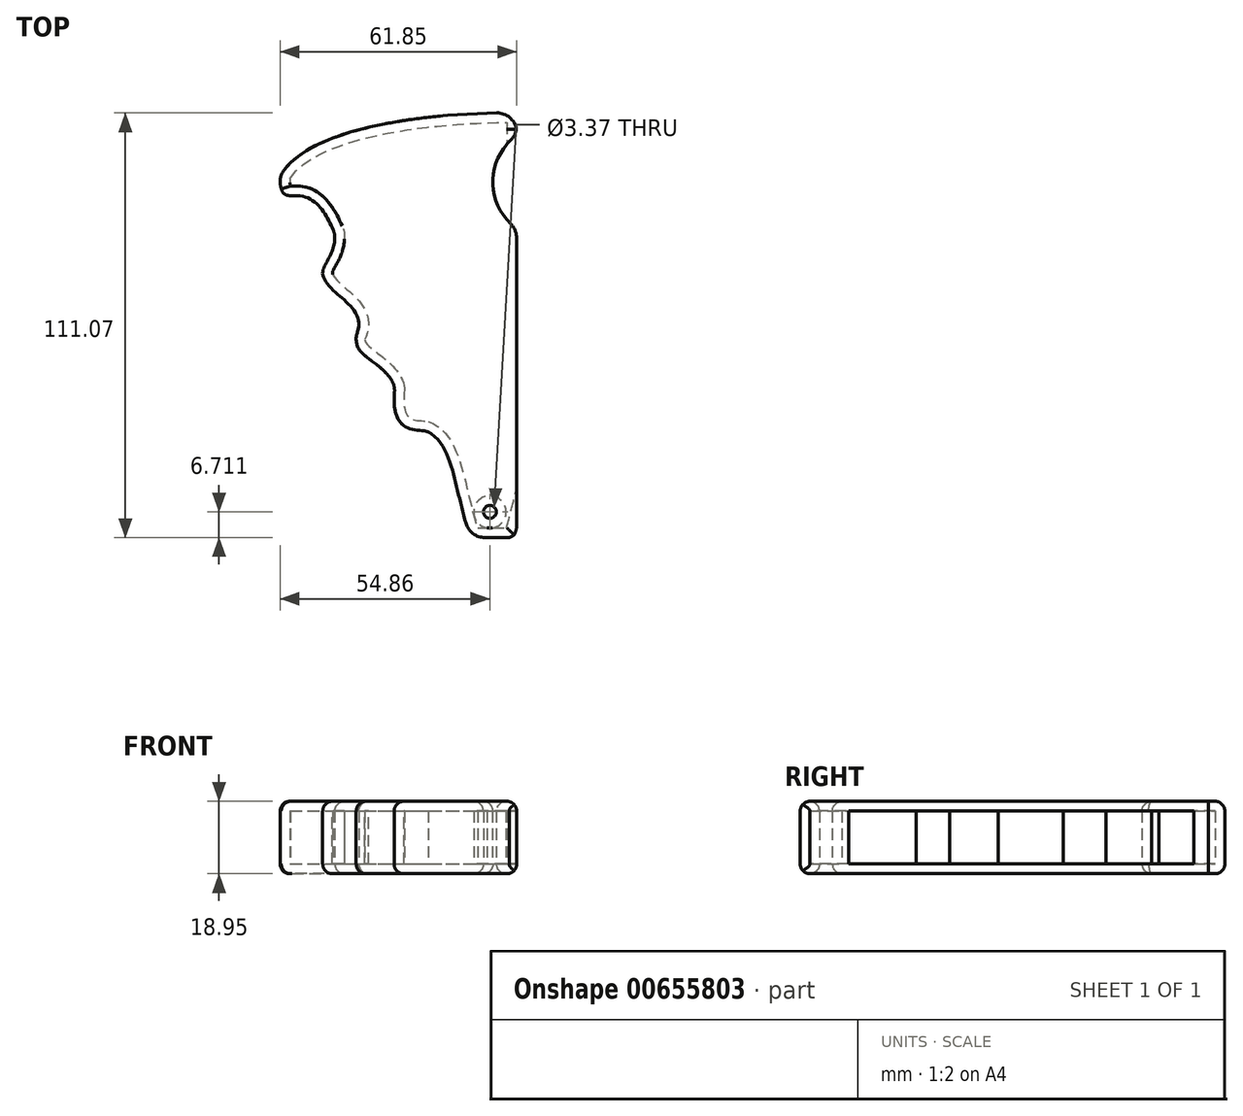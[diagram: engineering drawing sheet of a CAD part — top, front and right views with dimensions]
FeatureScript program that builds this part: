
annotation { "Feature Type Name" : "Feature", "Feature Type Description" : "" }
export const myFeature = defineFeature(function(context is Context, id is Id, definition is map)
    precondition{}
    {
        {
            var Q0;
            Q0=qCreatedBy(makeId("Top.planeOp"),FACE);
            var sketch = newSketch(context, id + "F0", { "sketchPlane" : qUnion([Q0])});
            skLineSegment(sketch, "E0.bottom", {"start": v(-30.91, 55.7) * mm, "end": v(31, 55.7) * mm});
            skLineSegment(sketch, "E0.top", {"start": v(-30.91, -55.42) * mm, "end": v(31, -55.42) * mm});
            skLineSegment(sketch, "E0.left", {"start": v(-30.91, 55.7) * mm, "end": v(-30.91, -55.42) * mm});
            skLineSegment(sketch, "E0.right", {"start": v(31, 55.7) * mm, "end": v(31, -55.42) * mm});
            skPoint(sketch, "E1", {"position": v(-30.91, 39.04) * mm});
            skPoint(sketch, "E2", {"position": v(31, 50.15) * mm});
            skPoint(sketch, "E3", {"position": v(31, 24.75) * mm});
            skCircle(sketch, "E4", {"center": v(40.03, 37.59) * mm, "radius": 15.24 * mm});
            skFitSpline(sketch, "E5", {"points": [v(-30.91, 39.04) * mm, v(31, 55.7) * mm], "startDerivative": vector(17.2, 32.72) * mm, "endDerivative": vector(93, 0) * mm});
            skFitSpline(sketch, "E6", {"points": [v(-30.91, 39.04) * mm, v(-16.57, 24.07) * mm], "startDerivative": vector(0, -34.25) * mm, "endDerivative": vector(21.47, -53.67) * mm});
            skFitSpline(sketch, "E7", {"points": [v(-16.57, 24.07) * mm, v(-19.33, 12.26) * mm], "startDerivative": vector(1.02, -19.93) * mm, "endDerivative": vector(5.41, -10.48) * mm});
            skFitSpline(sketch, "E8", {"points": [v(-19.33, 12.26) * mm, v(-11.02, -2.64) * mm], "startDerivative": vector(7.14, -14.54) * mm, "endDerivative": vector(-10.22, -21.72) * mm});
            skFitSpline(sketch, "E9", {"points": [v(31, -52.9) * mm, v(29.08, -55.42) * mm], "startDerivative": vector(-1.5, -5.77) * mm, "endDerivative": vector(-4.25, -1.78) * mm});
            skFitSpline(sketch, "E10", {"points": [v(-11.02, -2.64) * mm, v(-0.84, -16.46) * mm], "startDerivative": vector(-6.03, -15.08) * mm, "endDerivative": vector(3.58, -19.17) * mm});
            skFitSpline(sketch, "E11", {"points": [v(-0.84, -16.46) * mm, v(7.24, -27.52) * mm], "startDerivative": vector(-4.38, -35.2) * mm, "endDerivative": vector(7.67, -1.02) * mm});
            skFitSpline(sketch, "E12", {"points": [v(7.24, -27.52) * mm, v(19, -55.42) * mm], "startDerivative": vector(22.5, -8.69) * mm, "endDerivative": vector(12.78, -34.12) * mm});
            skCircle(sketch, "E13", {"center": v(24, -48.7) * mm, "radius": 1.69 * mm});
            skSolve(sketch);
        }
        {
            var Q0;
            {var subQ1=sQuery(id+"F0.wireOp",EDGE,"E5");Q0=makeQuery(id+"F0.imprint","IMPRINT",FACE,{"disambiguationData":[TD([[makeQuery(id+"F0.imprint","IMPRINT",EDGE,{"derivedFrom":subQ1}),-1.0]])]});}
            extrude(context, id + "F1", {"entities" : qUnion([Q0]), "depth" : 18.95 * mm, "offsetDistance" : 25.4 * mm});
        }
        {
            var Q0;
            Q0=makeQuery(id+"F1.opExtrude","SWEPT_FACE",FACE,{"disambiguationData":[OSD([sQuery(id+"F0.wireOp",EDGE,"E4")])]});
            var Q1;
            {var subQ0=sQuery(id+"F0.wireOp",EDGE,"E0.right");Q1=makeQuery(id+"F1.opExtrude","SWEPT_FACE",FACE,{"disambiguationData":[OSD([subQ0]),TDD([makeQuery(id+"F0.imprint","IMPRINT",EDGE,{"disambiguationData":[TD([[makeQuery(id+"F0.imprint","INTERSECT",VERTEX,{"derivedFrom":[subQ0,sQuery(id+"F0.wireOp",EDGE,"E9")]}),1.0]])],"derivedFrom":subQ0})])]});}
            shell(context, id + "F2", {"entities" : qUnion([Q0, Q1]), "thickness" : 2.54 * mm});
        }
        {
            var Q0;
            Q0=makeQuery(id+"F1.opExtrude","SWEPT_EDGE",EDGE,{"disambiguationData":[OSD([sQuery(id+"F0.wireOp",EDGE,"E0.left"),sQuery(id+"F0.wireOp",EDGE,"E5"),sQuery(id+"F0.wireOp",EDGE,"E6")])]});
            var Q1;
            Q1=makeQuery(id+"F1.opExtrude","SWEPT_EDGE",EDGE,{"disambiguationData":[OSD([sQuery(id+"F0.wireOp",EDGE,"E6"),sQuery(id+"F0.wireOp",EDGE,"E7")])]});
            var Q2;
            Q2=makeQuery(id+"F1.opExtrude","SWEPT_EDGE",EDGE,{"disambiguationData":[OSD([sQuery(id+"F0.wireOp",EDGE,"E7"),sQuery(id+"F0.wireOp",EDGE,"E8")])]});
            var Q3;
            Q3=makeQuery(id+"F1.opExtrude","SWEPT_EDGE",EDGE,{"disambiguationData":[OSD([sQuery(id+"F0.wireOp",EDGE,"E8"),sQuery(id+"F0.wireOp",EDGE,"E10")])]});
            var Q4;
            Q4=makeQuery(id+"F1.opExtrude","SWEPT_EDGE",EDGE,{"disambiguationData":[OSD([sQuery(id+"F0.wireOp",EDGE,"E10"),sQuery(id+"F0.wireOp",EDGE,"E11")])]});
            var Q5;
            Q5=makeQuery(id+"F1.opExtrude","SWEPT_EDGE",EDGE,{"disambiguationData":[OSD([sQuery(id+"F0.wireOp",EDGE,"E11"),sQuery(id+"F0.wireOp",EDGE,"E12")])]});
            var Q6;
            Q6=makeQuery(id+"F1.opExtrude","SWEPT_EDGE",EDGE,{"disambiguationData":[OSD([sQuery(id+"F0.wireOp",EDGE,"E0.top"),sQuery(id+"F0.wireOp",EDGE,"E12")])]});
            fillet(context, id + "F3", {"entities" : qUnion([Q0, Q1, Q2, Q3, Q4, Q5, Q6]), "radius" : 5.08 * mm, "tangentPropagation" : true, "allowEdgeOverflow" : false});
        }
        {
            var Q0;
            {var subQ0=sQuery(id+"F0.wireOp",EDGE,"E4");var subQ1=sQuery(id+"F0.wireOp",EDGE,"E0.right");Q0=makeQuery(id+"F2.opShell","OFFSET_EDGE",EDGE,{"disambiguationData":[OSD([subQ1,subQ0]),TDD([makeQuery(id+"F1.opExtrude","SWEPT_EDGE",EDGE,{"disambiguationData":[OSD([subQ1,subQ0]),TDD([makeQuery(id+"F0.imprint","INTERSECT",VERTEX,{"disambiguationData":[OD(1.0)],"derivedFrom":[subQ1,subQ0]})])]})])]});}
            var Q1;
            {var subQ0=sQuery(id+"F0.wireOp",EDGE,"E4");var subQ1=sQuery(id+"F0.wireOp",EDGE,"E0.right");Q1=makeQuery(id+"F1.opExtrude","SWEPT_EDGE",EDGE,{"disambiguationData":[OSD([subQ1,subQ0]),TDD([makeQuery(id+"F0.imprint","INTERSECT",VERTEX,{"disambiguationData":[OD(1.0)],"derivedFrom":[subQ1,subQ0]})])]});}
            var Q2;
            {var subQ0=sQuery(id+"F0.wireOp",EDGE,"E4");var subQ1=sQuery(id+"F0.wireOp",EDGE,"E0.right");Q2=makeQuery(id+"F1.opExtrude","SWEPT_EDGE",EDGE,{"disambiguationData":[OSD([subQ1,subQ0]),TDD([makeQuery(id+"F0.imprint","INTERSECT",VERTEX,{"disambiguationData":[OD(0.0)],"derivedFrom":[subQ1,subQ0]})])]});}
            var Q3;
            Q3=makeQuery(id+"F1.opExtrude","SWEPT_EDGE",EDGE,{"disambiguationData":[OSD([sQuery(id+"F0.wireOp",EDGE,"E0.bottom"),sQuery(id+"F0.wireOp",EDGE,"E0.right"),sQuery(id+"F0.wireOp",EDGE,"E5")])]});
            fillet(context, id + "F4", {"entities" : qUnion([Q0, Q1, Q2, Q3]), "radius" : 5.08 * mm, "tangentPropagation" : true, "allowEdgeOverflow" : false});
        }
        {
            var Q0;
            Q0=makeQuery(id+"F1.opExtrude","CAP_FACE",FACE,{"disambiguationData":[OSD([sQuery(id+"F0.wireOp",EDGE,"E0.top"),sQuery(id+"F0.wireOp",EDGE,"E0.right"),sQuery(id+"F0.wireOp",EDGE,"E4"),sQuery(id+"F0.wireOp",EDGE,"E5"),sQuery(id+"F0.wireOp",EDGE,"E6"),sQuery(id+"F0.wireOp",EDGE,"E7"),sQuery(id+"F0.wireOp",EDGE,"E8"),sQuery(id+"F0.wireOp",EDGE,"E9"),sQuery(id+"F0.wireOp",EDGE,"E10"),sQuery(id+"F0.wireOp",EDGE,"E11"),sQuery(id+"F0.wireOp",EDGE,"E12"),sQuery(id+"F0.wireOp",EDGE,"E13")])],"isStart":false});
            var Q1;
            Q1=makeQuery(id+"F1.opExtrude","CAP_FACE",FACE,{"disambiguationData":[OSD([sQuery(id+"F0.wireOp",EDGE,"E0.top"),sQuery(id+"F0.wireOp",EDGE,"E0.right"),sQuery(id+"F0.wireOp",EDGE,"E4"),sQuery(id+"F0.wireOp",EDGE,"E5"),sQuery(id+"F0.wireOp",EDGE,"E6"),sQuery(id+"F0.wireOp",EDGE,"E7"),sQuery(id+"F0.wireOp",EDGE,"E8"),sQuery(id+"F0.wireOp",EDGE,"E9"),sQuery(id+"F0.wireOp",EDGE,"E10"),sQuery(id+"F0.wireOp",EDGE,"E11"),sQuery(id+"F0.wireOp",EDGE,"E12"),sQuery(id+"F0.wireOp",EDGE,"E13")])],"isStart":true});
            fillet(context, id + "F5", {"entities" : qUnion([Q0, Q1]), "radius" : 2.54 * mm, "tangentPropagation" : true, "allowEdgeOverflow" : false});
        }
    });
